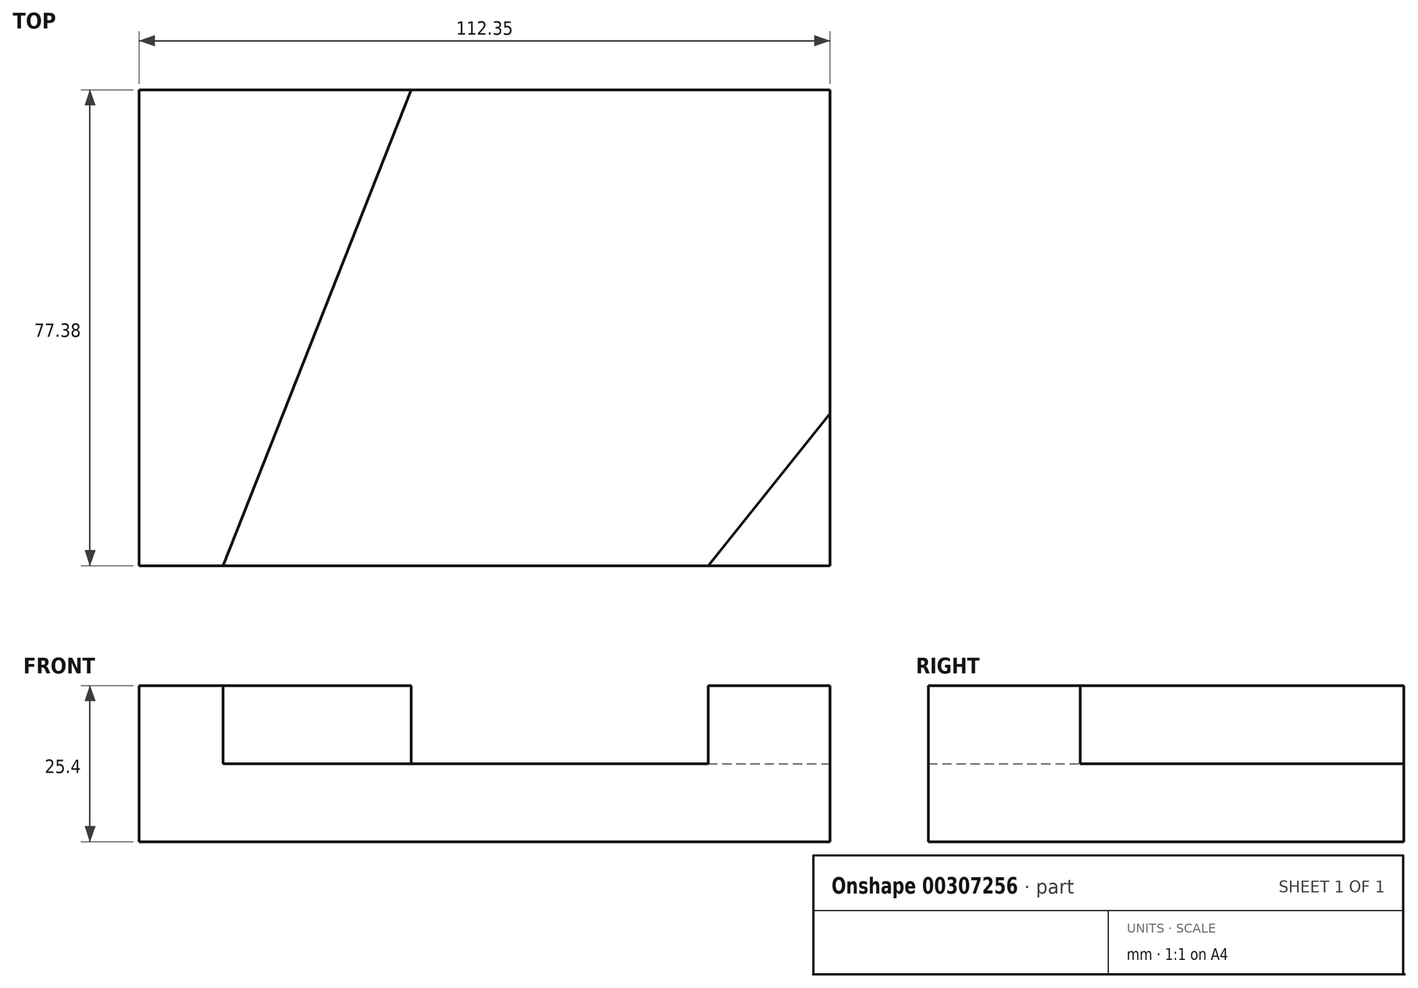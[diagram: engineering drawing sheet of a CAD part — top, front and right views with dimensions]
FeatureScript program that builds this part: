
annotation { "Feature Type Name" : "Feature", "Feature Type Description" : "" }
export const myFeature = defineFeature(function(context is Context, id is Id, definition is map)
    precondition{}
    {
        {
            var Q0;
            Q0=qCreatedBy(makeId("Top.planeOp"),FACE);
            var sketch = newSketch(context, id + "F0", { "sketchPlane" : qUnion([Q0])});
            skLineSegment(sketch, "E0", {"start": v(-37.14, -47.51) * mm, "end": v(55.1, -47.51) * mm});
            skLineSegment(sketch, "E1", {"start": v(55.1, -47.51) * mm, "end": v(55.1, 29.87) * mm});
            skLineSegment(sketch, "E2", {"start": v(55.1, 29.87) * mm, "end": v(-57.26, 29.87) * mm});
            skLineSegment(sketch, "E3", {"start": v(-57.26, 29.87) * mm, "end": v(-57.26, -47.51) * mm});
            skLineSegment(sketch, "E4", {"start": v(-57.26, -47.51) * mm, "end": v(-37.14, -47.51) * mm});
            skSolve(sketch);
        }
        {
            var Q0;
            Q0=makeQuery(id+"F0.imprint","IMPRINT",FACE,{"disambiguationData":[TD([[makeQuery(id+"F0.imprint","IMPRINT",EDGE,{"derivedFrom":sQuery(id+"F0.wireOp",EDGE,"E0")}),1.0]])]});
            extrude(context, id + "F1", {"entities" : qUnion([Q0]), "depth" : 12.7 * mm});
        }
        {
            var Q0;
            Q0=makeQuery(id+"F1.opExtrude","CAP_FACE",FACE,{"disambiguationData":[OSD([sQuery(id+"F0.wireOp",EDGE,"E0"),sQuery(id+"F0.wireOp",EDGE,"E1"),sQuery(id+"F0.wireOp",EDGE,"E2"),sQuery(id+"F0.wireOp",EDGE,"E3"),sQuery(id+"F0.wireOp",EDGE,"E4")])],"isStart":false});
            var sketch = newSketch(context, id + "F2", { "sketchPlane" : qUnion([Q0])});
            skLineSegment(sketch, "E5", {"start": v(-13, 29.87) * mm, "end": v(-43.64, -47.51) * mm});
            skLineSegment(sketch, "E6", {"start": v(32.8, -47.51) * mm, "end": v(55.1, -23.99) * mm});
            skLineSegment(sketch, "E7", {"start": v(55.1, -23.99) * mm, "end": v(55.1, -47.51) * mm});
            skLineSegment(sketch, "E8", {"start": v(55.1, -47.51) * mm, "end": v(32.8, -47.51) * mm});
            skLineSegment(sketch, "E9", {"start": v(-43.64, -47.51) * mm, "end": v(-57.26, -47.51) * mm});
            skLineSegment(sketch, "E10", {"start": v(-57.26, -47.51) * mm, "end": v(-57.26, 29.87) * mm});
            skLineSegment(sketch, "E11", {"start": v(-57.26, 29.87) * mm, "end": v(-13, 29.87) * mm});
            skSolve(sketch);
        }
        {
            var Q0;
            Q0=makeQuery(id+"F2.imprint","IMPRINT",FACE,{"disambiguationData":[TD([[makeQuery(id+"F2.imprint","IMPRINT",EDGE,{"derivedFrom":sQuery(id+"F2.wireOp",EDGE,"E5")}),-1.0]])]});
            extrude(context, id + "F3", {"entities" : qUnion([Q0]), "operationType" : NewBodyOperationType.ADD, "depth" : 12.7 * mm});
        }
        {
            var Q0;
            Q0=makeQuery(id+"F1.opExtrude","CAP_FACE",FACE,{"disambiguationData":[OSD([sQuery(id+"F0.wireOp",EDGE,"E0"),sQuery(id+"F0.wireOp",EDGE,"E1"),sQuery(id+"F0.wireOp",EDGE,"E2"),sQuery(id+"F0.wireOp",EDGE,"E3"),sQuery(id+"F0.wireOp",EDGE,"E4")])],"isStart":false});
            var sketch = newSketch(context, id + "F4", { "sketchPlane" : qUnion([Q0])});
            skLineSegment(sketch, "E12", {"start": v(35.28, -47.51) * mm, "end": v(55.1, -22.75) * mm});
            skLineSegment(sketch, "E13", {"start": v(55.1, -22.75) * mm, "end": v(55.1, -47.51) * mm});
            skLineSegment(sketch, "E14", {"start": v(55.1, -47.51) * mm, "end": v(35.28, -47.51) * mm});
            skSolve(sketch);
        }
        {
            var Q0;
            Q0=makeQuery(id+"F4.imprint","IMPRINT",FACE,{"disambiguationData":[TD([[makeQuery(id+"F4.imprint","IMPRINT",EDGE,{"derivedFrom":sQuery(id+"F4.wireOp",EDGE,"E12")}),-1.0]])]});
            extrude(context, id + "F5", {"entities" : qUnion([Q0]), "operationType" : NewBodyOperationType.ADD, "depth" : 12.7 * mm});
        }
    });
